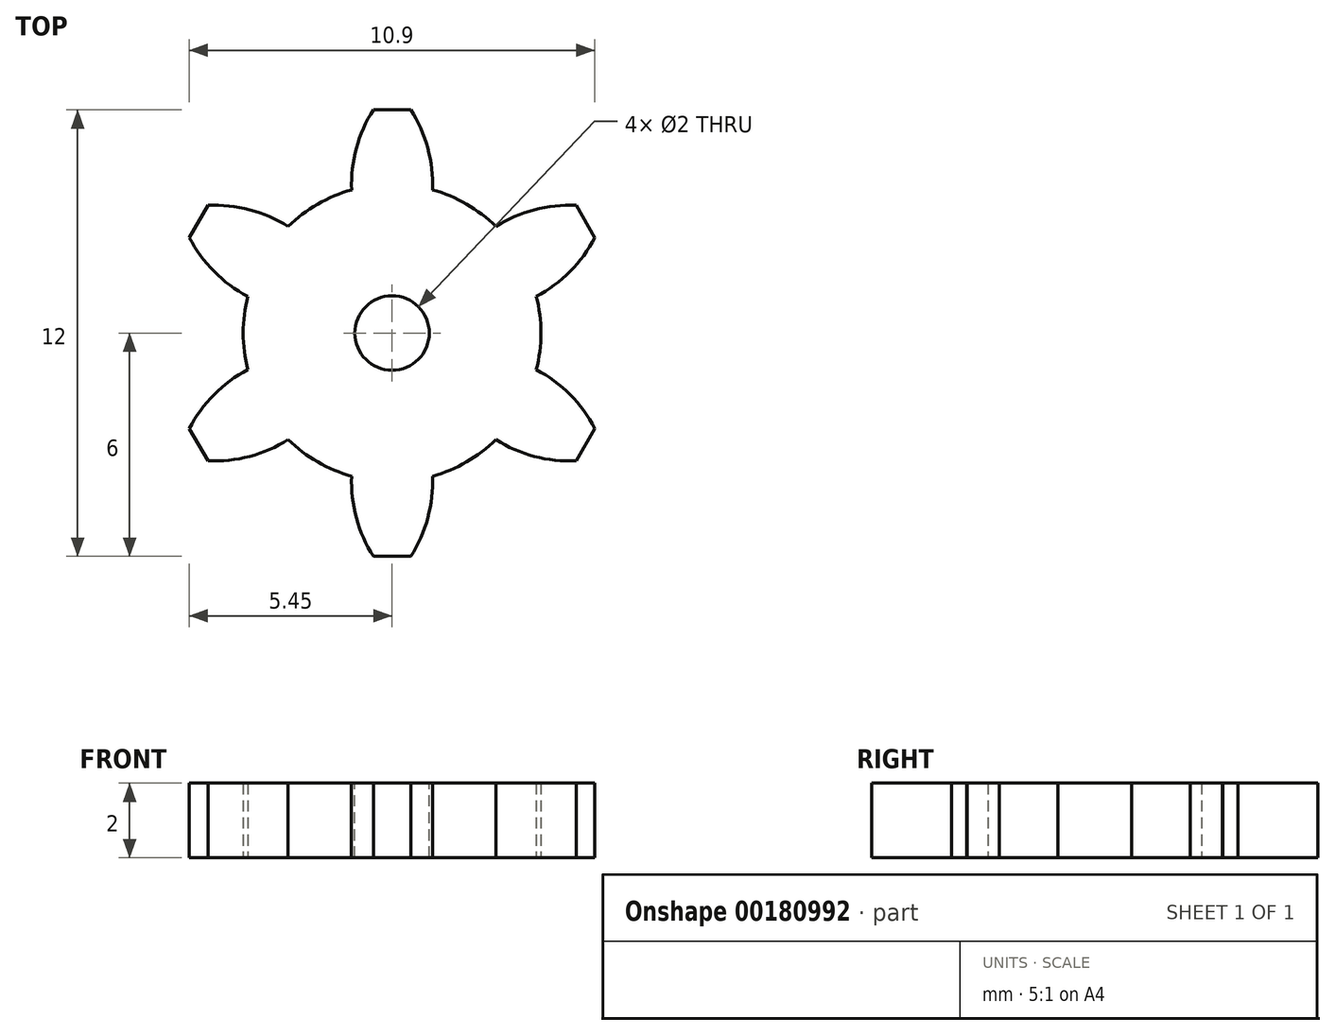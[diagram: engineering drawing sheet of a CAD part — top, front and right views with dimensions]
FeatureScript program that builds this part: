
annotation { "Feature Type Name" : "Feature", "Feature Type Description" : "" }
export const myFeature = defineFeature(function(context is Context, id is Id, definition is map)
    precondition{}
    {
        {
            var Q0;
            Q0=qCreatedBy(makeId("Top.planeOp"),FACE);
            var sketch = newSketch(context, id + "F0", { "sketchPlane" : qUnion([Q0])});
            skCircle(sketch, "E0", {"center": v(0, 0) * mm, "radius": 4 * mm});
            skLineSegment(sketch, "E1", {"start": v(0, 0) * mm, "end": v(0, 4) * mm, "construction": true});
            skLineSegment(sketch, "E2", {"start": v(0, 4) * mm, "end": v(0, 6) * mm});
            skLineSegment(sketch, "E3", {"start": v(0, 6) * mm, "end": v(-0.5, 6) * mm});
            skArc(sketch, "E4", {"start": v(-0.5, 6) * mm, "mid": v(-0.96, 4.97) * mm, "end": v(-1.09, 3.85) * mm});
            skLineSegment(sketch, "E5.MirrorCS", {"start": v(0, 6) * mm, "end": v(0.5, 6) * mm});
            skArc(sketch, "E6.MirrorCS", {"start": v(0.5, 6) * mm, "mid": v(0.96, 4.97) * mm, "end": v(1.09, 3.85) * mm});
            skArc(sketch, "E7.1.0", {"start": v(-5.45, 2.57) * mm, "mid": v(-4.78, 1.65) * mm, "end": v(-3.88, 0.98) * mm});
            skLineSegment(sketch, "E7.1.1", {"start": v(-5.2, 3) * mm, "end": v(-5.45, 2.57) * mm});
            skLineSegment(sketch, "E7.1.2", {"start": v(-5.2, 3) * mm, "end": v(-4.95, 3.43) * mm});
            skArc(sketch, "E7.1.3", {"start": v(-4.95, 3.43) * mm, "mid": v(-3.82, 3.32) * mm, "end": v(-2.8, 2.87) * mm});
            skArc(sketch, "E7.2.0", {"start": v(-4.95, -3.43) * mm, "mid": v(-3.82, -3.32) * mm, "end": v(-2.8, -2.87) * mm});
            skLineSegment(sketch, "E7.2.1", {"start": v(-5.2, -3) * mm, "end": v(-4.95, -3.43) * mm});
            skLineSegment(sketch, "E7.2.2", {"start": v(-5.2, -3) * mm, "end": v(-5.45, -2.57) * mm});
            skArc(sketch, "E7.2.3", {"start": v(-5.45, -2.57) * mm, "mid": v(-4.78, -1.65) * mm, "end": v(-3.88, -0.98) * mm});
            skArc(sketch, "E7.3.0", {"start": v(0.5, -6) * mm, "mid": v(0.96, -4.97) * mm, "end": v(1.09, -3.85) * mm});
            skLineSegment(sketch, "E7.3.1", {"start": v(0, -6) * mm, "end": v(0.5, -6) * mm});
            skLineSegment(sketch, "E7.3.2", {"start": v(0, -6) * mm, "end": v(-0.5, -6) * mm});
            skArc(sketch, "E7.3.3", {"start": v(-0.5, -6) * mm, "mid": v(-0.96, -4.97) * mm, "end": v(-1.09, -3.85) * mm});
            skArc(sketch, "E7.4.0", {"start": v(5.45, -2.57) * mm, "mid": v(4.78, -1.65) * mm, "end": v(3.88, -0.98) * mm});
            skLineSegment(sketch, "E7.4.1", {"start": v(5.2, -3) * mm, "end": v(5.45, -2.57) * mm});
            skLineSegment(sketch, "E7.4.2", {"start": v(5.2, -3) * mm, "end": v(4.95, -3.43) * mm});
            skArc(sketch, "E7.4.3", {"start": v(4.95, -3.43) * mm, "mid": v(3.82, -3.32) * mm, "end": v(2.8, -2.87) * mm});
            skArc(sketch, "E7.5.0", {"start": v(4.95, 3.43) * mm, "mid": v(3.82, 3.32) * mm, "end": v(2.8, 2.87) * mm});
            skLineSegment(sketch, "E7.5.1", {"start": v(5.2, 3) * mm, "end": v(4.95, 3.43) * mm});
            skLineSegment(sketch, "E7.5.2", {"start": v(5.2, 3) * mm, "end": v(5.45, 2.57) * mm});
            skArc(sketch, "E7.5.3", {"start": v(5.45, 2.57) * mm, "mid": v(4.78, 1.65) * mm, "end": v(3.88, 0.98) * mm});
            skSolve(sketch);
        }
        {
            var Q0;
            Q0=qSketchRegion(id+"F0",true);
            extrude(context, id + "F1", {"entities" : qUnion([Q0]), "depth" : 2 * mm});
        }
        {
            var Q0;
            Q0=makeQuery(id+"F1.opExtrude","CAP_FACE",FACE,{"disambiguationData":[OSD([sQuery(id+"F0.wireOp",EDGE,"E0"),sQuery(id+"F0.wireOp",EDGE,"E3"),sQuery(id+"F0.wireOp",EDGE,"E4"),sQuery(id+"F0.wireOp",EDGE,"E5.MirrorCS"),sQuery(id+"F0.wireOp",EDGE,"E6.MirrorCS"),sQuery(id+"F0.wireOp",EDGE,"E7.1.0"),sQuery(id+"F0.wireOp",EDGE,"E7.1.1"),sQuery(id+"F0.wireOp",EDGE,"E7.1.2"),sQuery(id+"F0.wireOp",EDGE,"E7.1.3"),sQuery(id+"F0.wireOp",EDGE,"E7.2.0"),sQuery(id+"F0.wireOp",EDGE,"E7.2.1"),sQuery(id+"F0.wireOp",EDGE,"E7.2.2"),sQuery(id+"F0.wireOp",EDGE,"E7.2.3"),sQuery(id+"F0.wireOp",EDGE,"E7.3.0"),sQuery(id+"F0.wireOp",EDGE,"E7.3.1"),sQuery(id+"F0.wireOp",EDGE,"E7.3.2"),sQuery(id+"F0.wireOp",EDGE,"E7.3.3"),sQuery(id+"F0.wireOp",EDGE,"E7.4.0"),sQuery(id+"F0.wireOp",EDGE,"E7.4.1"),sQuery(id+"F0.wireOp",EDGE,"E7.4.2"),sQuery(id+"F0.wireOp",EDGE,"E7.4.3"),sQuery(id+"F0.wireOp",EDGE,"E7.5.0"),sQuery(id+"F0.wireOp",EDGE,"E7.5.1"),sQuery(id+"F0.wireOp",EDGE,"E7.5.2"),sQuery(id+"F0.wireOp",EDGE,"E7.5.3"),sQuery(id+"F0.wireOp",EDGE,"E7.6.0"),sQuery(id+"F0.wireOp",EDGE,"E7.6.1"),sQuery(id+"F0.wireOp",EDGE,"E7.6.2"),sQuery(id+"F0.wireOp",EDGE,"E7.6.3"),sQuery(id+"F0.wireOp",EDGE,"E7.7.0"),sQuery(id+"F0.wireOp",EDGE,"E7.7.1"),sQuery(id+"F0.wireOp",EDGE,"E7.7.2"),sQuery(id+"F0.wireOp",EDGE,"E7.7.3")])],"isStart":false});
            var sketch = newSketch(context, id + "F2", { "sketchPlane" : qUnion([Q0])});
            skCircle(sketch, "E8", {"center": v(0, 0) * mm, "radius": 1 * mm});
            skSolve(sketch);
        }
        {
            var Q0;
            Q0=qSketchRegion(id+"F2",true);
            extrude(context, id + "F3", {"entities" : qUnion([Q0]), "operationType" : NewBodyOperationType.REMOVE, "endBound" : BoundingType.THROUGH_ALL, "oppositeDirection" : true, "depth" : 25 * mm});
        }
    });
